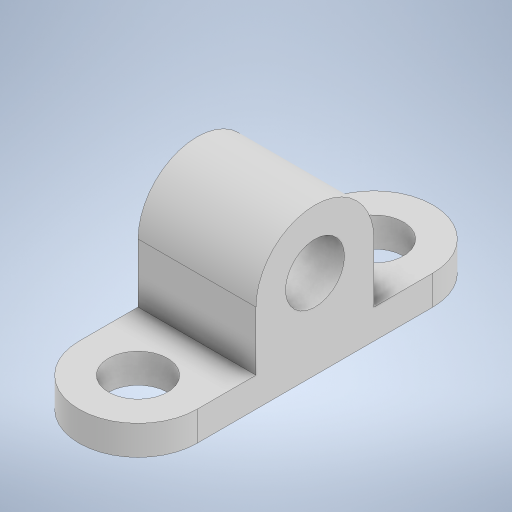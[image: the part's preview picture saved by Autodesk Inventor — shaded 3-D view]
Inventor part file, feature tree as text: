
AUTODESK INVENTOR PART (.ipt)
format: ipt  version: 2024 (Build 280153000, 153)  size: 257,536 bytes
history: native  units: mm
features: extrude x2, sketch x2, other x1
ambient origin geometry x8: Origin, YZ Plane, XZ Plane, XY Plane, X Axis, Y Axis, Z Axis, Center Point
bodies: Body1 (feature_tree)
feature tree (5):
  other  "Sólido1"
  extrude  "Extrusión1"  Depth=20.0mm
  extrude  "Extrusión2"  Depth=20.0mm
  sketch  "Boceto1"  dims[d1=40.0mm d3=20.0mm]
  sketch  "Boceto2"  dims[d4=40.0mm d6=20.0mm d7=40.0mm d8=10.0mm d9=0.0mm d12=40.0mm d13=20.0mm d14=40.0mm d15=0.0mm]
